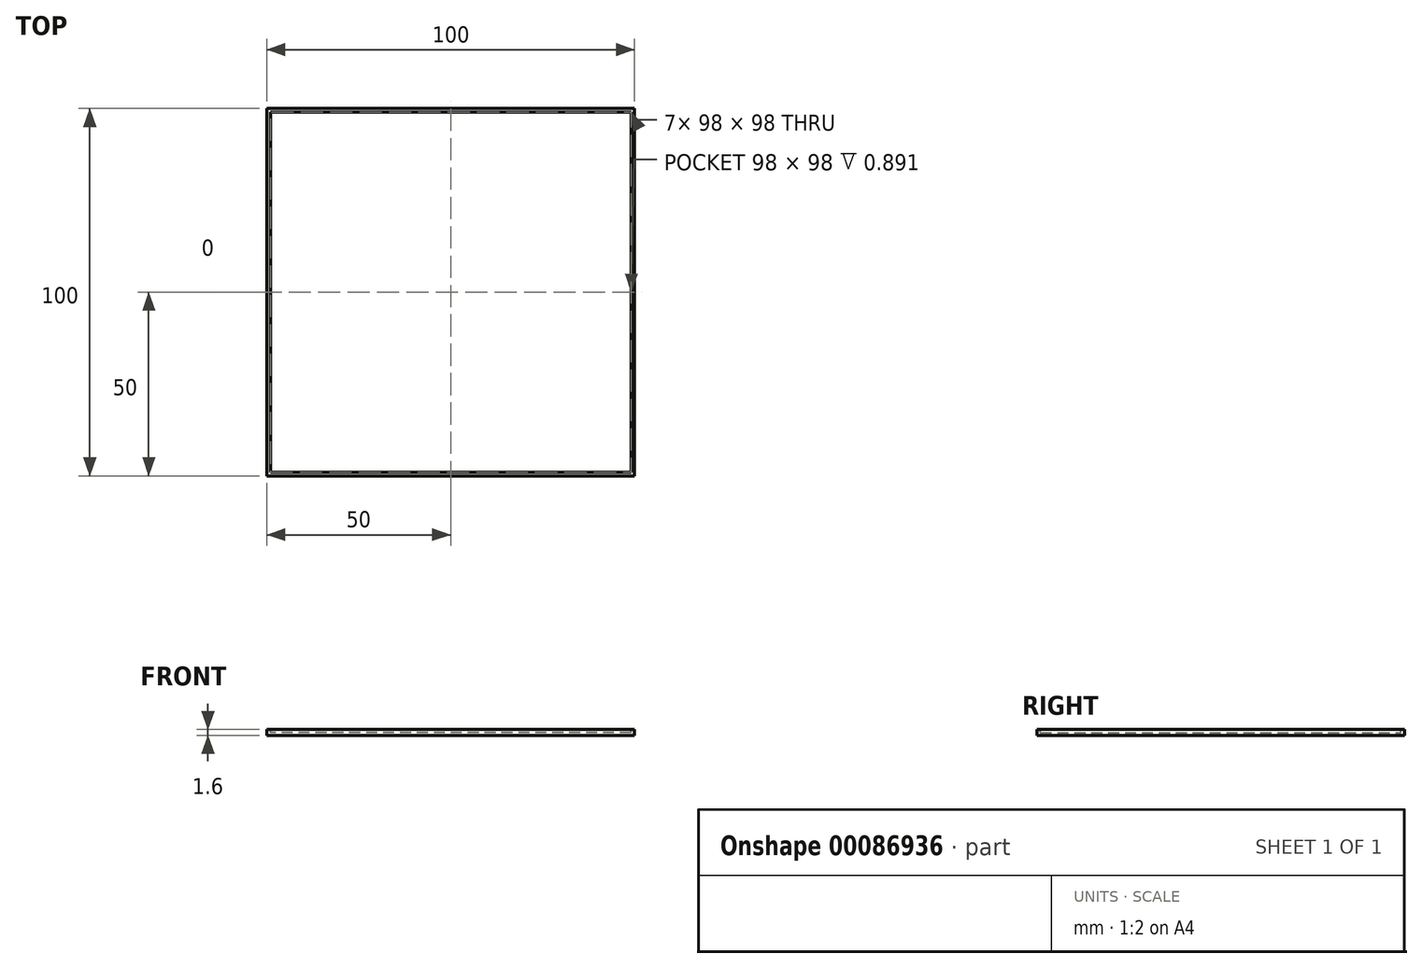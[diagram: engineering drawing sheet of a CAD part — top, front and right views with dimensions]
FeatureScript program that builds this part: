
annotation { "Feature Type Name" : "Feature", "Feature Type Description" : "" }
export const myFeature = defineFeature(function(context is Context, id is Id, definition is map)
    precondition{}
    {
        {
            var Q0;
            Q0=qCreatedBy(makeId("Top.planeOp"),FACE);
            var sketch = newSketch(context, id + "F0", { "sketchPlane" : qUnion([Q0])});
            skLineSegment(sketch, "E0.bottom", {"start": v(50, -50) * mm, "end": v(-50, -50) * mm});
            skLineSegment(sketch, "E0.top", {"start": v(50, 50) * mm, "end": v(-50, 50) * mm});
            skLineSegment(sketch, "E0.left", {"start": v(50, -50) * mm, "end": v(50, 50) * mm});
            skLineSegment(sketch, "E0.right", {"start": v(-50, -50) * mm, "end": v(-50, 50) * mm});
            skPoint(sketch, "E0.middle", {"position": v(0, 0) * mm});
            skSolve(sketch);
        }
        {
            var Q0;
            Q0=makeQuery(id+"F0.imprint","IMPRINT",FACE,{"disambiguationData":[TD([[makeQuery(id+"F0.imprint","IMPRINT",EDGE,{"derivedFrom":sQuery(id+"F0.wireOp",EDGE,"E0.bottom")}),-1.0]])]});
            extrude(context, id + "F1", {"entities" : qUnion([Q0]), "depth" : 1.6 * mm});
        }
        {
            var Q0;
            Q0=makeQuery(id+"F1.opExtrude","CAP_FACE",FACE,{"disambiguationData":[OSD([sQuery(id+"F0.wireOp",EDGE,"E0.bottom"),sQuery(id+"F0.wireOp",EDGE,"E0.top"),sQuery(id+"F0.wireOp",EDGE,"E0.left"),sQuery(id+"F0.wireOp",EDGE,"E0.right")])],"isStart":false});
            var sketch = newSketch(context, id + "F2", { "sketchPlane" : qUnion([Q0])});
            skLineSegment(sketch, "E1.bottom", {"start": v(49, -49) * mm, "end": v(-49, -49) * mm});
            skLineSegment(sketch, "E1.top", {"start": v(49, 49) * mm, "end": v(-49, 49) * mm});
            skLineSegment(sketch, "E1.left", {"start": v(49, -49) * mm, "end": v(49, 49) * mm});
            skLineSegment(sketch, "E1.right", {"start": v(-49, -49) * mm, "end": v(-49, 49) * mm});
            skPoint(sketch, "E1.middle", {"position": v(0, 0) * mm});
            skSolve(sketch);
        }
        {
            var Q0;
            Q0=makeQuery(id+"F2.imprint","IMPRINT",FACE,{"disambiguationData":[TD([[makeQuery(id+"F2.imprint","IMPRINT",EDGE,{"derivedFrom":sQuery(id+"F2.wireOp",EDGE,"E1.bottom")}),-1.0]])]});
            extrude(context, id + "F3", {"entities" : qUnion([Q0]), "operationType" : NewBodyOperationType.REMOVE, "oppositeDirection" : true, "depth" : 0.9 * mm});
        }
    });
